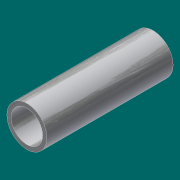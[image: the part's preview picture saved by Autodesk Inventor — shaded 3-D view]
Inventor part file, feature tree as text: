
AUTODESK INVENTOR PART (.ipt)
format: ipt  version: 2017 (Build 210142000, 142)  size: 88,576 bytes
history: native  units: in
note: dims shown in document units (in); Inventor stores cm internally (conversion verified against a paired STEP export)
features: extrude x1, sketch x1
ambient origin geometry x8: Origin, YZ Plane, XZ Plane, XY Plane, X Axis, Y Axis, Z Axis, Center Point
bodies: Solid1 (feature_tree)
feature tree (2):
  extrude  "Extrusion1"  Depth=6.0in
  sketch  "Sketch1"  dims[d0=1.9in d1=1.5in d2=6.0in d3=0.0in]
